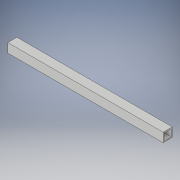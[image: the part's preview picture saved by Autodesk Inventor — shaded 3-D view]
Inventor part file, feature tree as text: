
AUTODESK INVENTOR PART (.ipt)
format: ipt  version: 2018 (Build 220112000, 112)  size: 97,792 bytes
history: native  units: in
note: dims shown in document units (in); Inventor stores cm internally (conversion verified against a paired STEP export)
features: extrude x1, sketch x1
ambient origin geometry x8: Origin, YZ Plane, XZ Plane, XY Plane, X Axis, Y Axis, Z Axis, Center Point
bodies: Solid1 (feature_tree)
feature tree (2):
  extrude  "Extrusion1"  Depth=1.0in
  sketch  "Sketch1"  dims[d0=1.0in d1=1.0in d2=0.125in d3=17.0in d4=0.0in]
